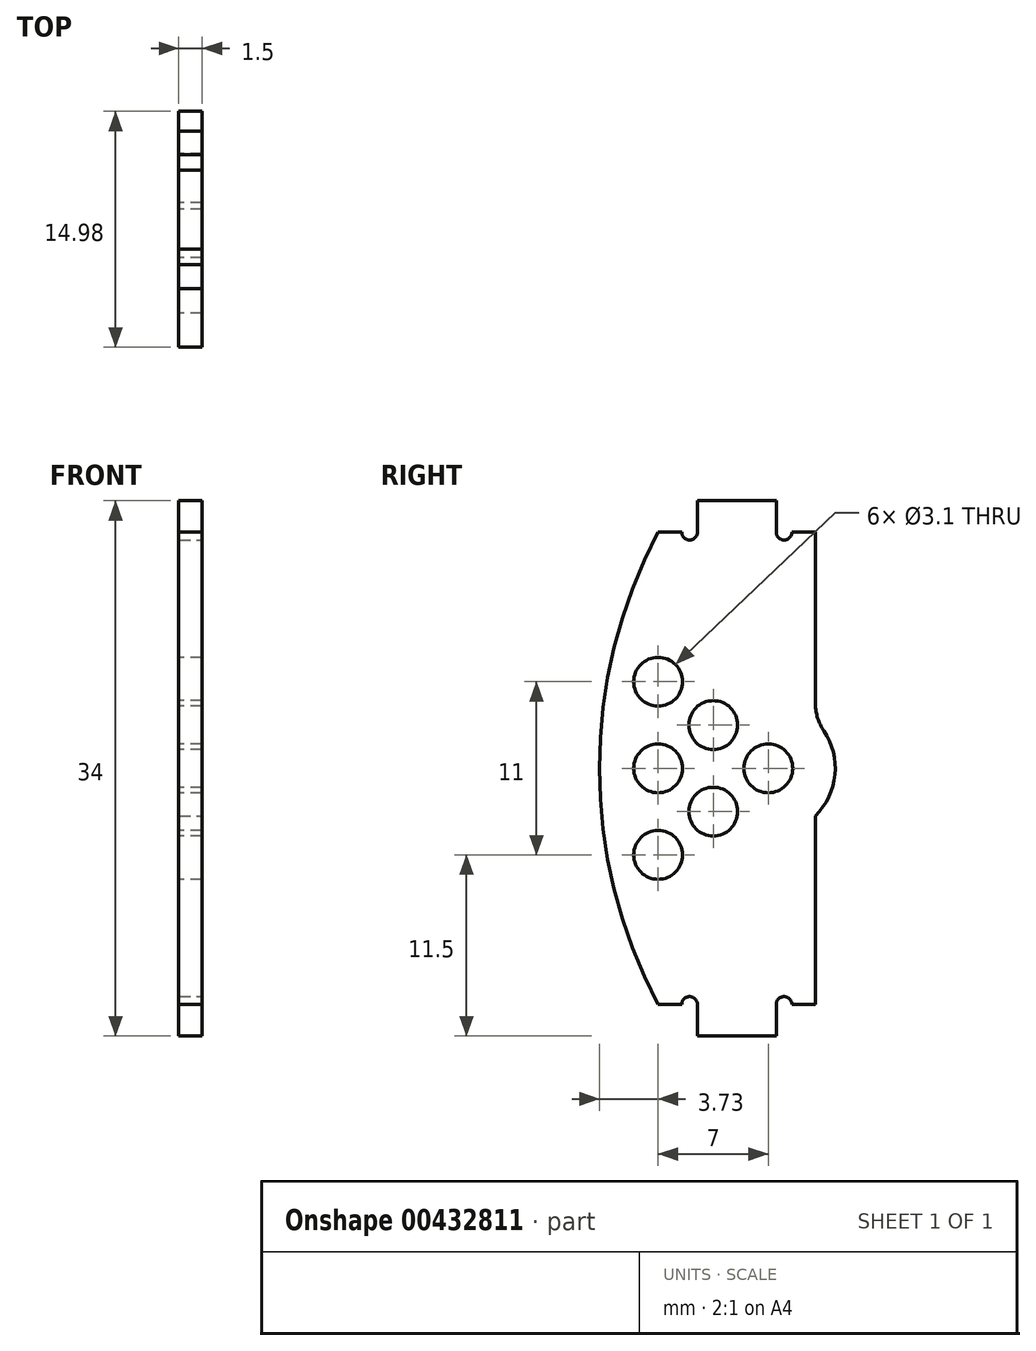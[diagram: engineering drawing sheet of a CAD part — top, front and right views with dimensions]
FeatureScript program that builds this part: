
annotation { "Feature Type Name" : "Feature", "Feature Type Description" : "" }
export const myFeature = defineFeature(function(context is Context, id is Id, definition is map)
    precondition{}
    {
        {
            var Q0;
            Q0=qCreatedBy(makeId("Right.planeOp"),FACE);
            var sketch = newSketch(context, id + "F0", { "sketchPlane" : qUnion([Q0])});
            skLineSegment(sketch, "E0", {"start": v(0, 0) * mm, "end": v(0, 30) * mm});
            skLineSegment(sketch, "E1", {"start": v(0, 30) * mm, "end": v(-10, 30) * mm});
            skLineSegment(sketch, "E2", {"start": v(0, 0) * mm, "end": v(-10, 0) * mm});
            skArc(sketch, "E3", {"start": v(-10, 30) * mm, "mid": v(-13.73, 15) * mm, "end": v(-10, 0) * mm});
            skCircle(sketch, "E4", {"center": v(-3, 15) * mm, "radius": 1.55 * mm});
            skLineSegment(sketch, "E5", {"start": v(-3, 15) * mm, "end": v(0, 15) * mm, "construction": true});
            skCircle(sketch, "E6", {"center": v(-10, 9.5) * mm, "radius": 1.55 * mm});
            skCircle(sketch, "E7.MirrorC", {"center": v(-10, 20.5) * mm, "radius": 1.55 * mm});
            skCircle(sketch, "E8", {"center": v(-6.5, 12.25) * mm, "radius": 1.55 * mm});
            skCircle(sketch, "E9.MirrorC", {"center": v(-6.5, 17.75) * mm, "radius": 1.55 * mm});
            skCircle(sketch, "E10", {"center": v(-10, 15) * mm, "radius": 1.55 * mm});
            skSolve(sketch);
        }
        {
            var Q0;
            Q0=makeQuery(id+"F0.imprint","IMPRINT",FACE,{"disambiguationData":[TD([[makeQuery(id+"F0.imprint","IMPRINT",EDGE,{"derivedFrom":sQuery(id+"F0.wireOp",EDGE,"E0")}),1.0]])]});
            extrude(context, id + "F1", {"entities" : qUnion([Q0]), "depth" : 1.5 * mm});
        }
        {
            var Q0;
            Q0=makeQuery(id+"F1.opExtrude","CAP_FACE",FACE,{"disambiguationData":[OSD([sQuery(id+"F0.wireOp",EDGE,"E0"),sQuery(id+"F0.wireOp",EDGE,"E1"),sQuery(id+"F0.wireOp",EDGE,"E2"),sQuery(id+"F0.wireOp",EDGE,"E3"),sQuery(id+"F0.wireOp",EDGE,"E4")])],"isStart":false});
            var sketch = newSketch(context, id + "F2", { "sketchPlane" : qUnion([Q0])});
            skLineSegment(sketch, "E11.bottom", {"start": v(-7.5, 30) * mm, "end": v(-2.5, 30) * mm});
            skLineSegment(sketch, "E11.top", {"start": v(-7.5, 32) * mm, "end": v(-2.5, 32) * mm});
            skLineSegment(sketch, "E11.left", {"start": v(-7.5, 30) * mm, "end": v(-7.5, 32) * mm});
            skLineSegment(sketch, "E11.right", {"start": v(-2.5, 30) * mm, "end": v(-2.5, 32) * mm});
            skLineSegment(sketch, "E12", {"start": v(-3, 15) * mm, "end": v(0, 15) * mm, "construction": true});
            skLineSegment(sketch, "E13.MirrorCS", {"start": v(-2.5, 0) * mm, "end": v(-2.5, -2) * mm});
            skLineSegment(sketch, "E14.MirrorCS", {"start": v(-7.5, 0) * mm, "end": v(-7.5, -2) * mm});
            skLineSegment(sketch, "E15.MirrorCS", {"start": v(-7.5, -2) * mm, "end": v(-2.5, -2) * mm});
            skLineSegment(sketch, "E16.MirrorCS", {"start": v(-7.5, 0) * mm, "end": v(-2.5, 0) * mm});
            skSolve(sketch);
        }
        {
            var Q0;
            Q0=makeQuery(id+"F2.imprint","IMPRINT",FACE,{"disambiguationData":[TD([[makeQuery(id+"F2.imprint","IMPRINT",EDGE,{"derivedFrom":sQuery(id+"F2.wireOp",EDGE,"E11.bottom")}),-1.0]])]});
            var Q1;
            Q1=makeQuery(id+"F2.imprint","IMPRINT",FACE,{"disambiguationData":[TD([[makeQuery(id+"F2.imprint","IMPRINT",EDGE,{"derivedFrom":sQuery(id+"F2.wireOp",EDGE,"E13.MirrorCS")}),-1.0]])]});
            extrude(context, id + "F3", {"entities" : qUnion([Q0, Q1]), "operationType" : NewBodyOperationType.ADD, "oppositeDirection" : true, "depth" : 1.5 * mm});
        }
        {
            var Q0;
            Q0=makeQuery(id+"F3.boolean.opBoolean","MERGE",FACE,{"derivedFrom":[makeQuery(id+"F1.opExtrude","CAP_FACE",FACE,{"disambiguationData":[OSD([sQuery(id+"F0.wireOp",EDGE,"E0"),sQuery(id+"F0.wireOp",EDGE,"E1"),sQuery(id+"F0.wireOp",EDGE,"E2"),sQuery(id+"F0.wireOp",EDGE,"E3"),sQuery(id+"F0.wireOp",EDGE,"E4")])],"isStart":false}),makeQuery(id+"F3.opExtrude","CAP_FACE",FACE,{"disambiguationData":[OSD([sQuery(id+"F2.wireOp",EDGE,"E11.bottom"),sQuery(id+"F2.wireOp",EDGE,"E11.top"),sQuery(id+"F2.wireOp",EDGE,"E11.left"),sQuery(id+"F2.wireOp",EDGE,"E11.right")])],"isStart":true}),makeQuery(id+"F3.opExtrude","CAP_FACE",FACE,{"disambiguationData":[OSD([sQuery(id+"F2.wireOp",EDGE,"E13.MirrorCS"),sQuery(id+"F2.wireOp",EDGE,"E14.MirrorCS"),sQuery(id+"F2.wireOp",EDGE,"E15.MirrorCS"),sQuery(id+"F2.wireOp",EDGE,"E16.MirrorCS")])],"isStart":true})]});
            var sketch = newSketch(context, id + "F4", { "sketchPlane" : qUnion([Q0])});
            skCircle(sketch, "E17", {"center": v(-8, 30) * mm, "radius": 0.5 * mm});
            skCircle(sketch, "E18", {"center": v(-2, 30) * mm, "radius": 0.5 * mm});
            skLineSegment(sketch, "E19", {"start": v(-3, 15) * mm, "end": v(0, 15) * mm, "construction": true});
            skCircle(sketch, "E20.MirrorC", {"center": v(-2, 0) * mm, "radius": 0.5 * mm});
            skCircle(sketch, "E21.MirrorC", {"center": v(-8, 0) * mm, "radius": 0.5 * mm});
            skSolve(sketch);
        }
        {
            var Q0;
            Q0 = qSketchRegion(id + "F4", true);
            extrude(context, id + "F5", {"entities" : qUnion([Q0]), "operationType" : NewBodyOperationType.REMOVE, "oppositeDirection" : true, "depth" : 25 * mm});
        }
        {
            var Q0;
            Q0=makeQuery(id+"F3.boolean.opBoolean","MERGE",FACE,{"derivedFrom":[makeQuery(id+"F1.opExtrude","CAP_FACE",FACE,{"disambiguationData":[OSD([sQuery(id+"F0.wireOp",EDGE,"E0"),sQuery(id+"F0.wireOp",EDGE,"E1"),sQuery(id+"F0.wireOp",EDGE,"E2"),sQuery(id+"F0.wireOp",EDGE,"E3"),sQuery(id+"F0.wireOp",EDGE,"E4"),sQuery(id+"F0.wireOp",EDGE,"E6")])],"isStart":false}),makeQuery(id+"F3.opExtrude","CAP_FACE",FACE,{"disambiguationData":[OSD([sQuery(id+"F2.wireOp",EDGE,"E11.bottom"),sQuery(id+"F2.wireOp",EDGE,"E11.top"),sQuery(id+"F2.wireOp",EDGE,"E11.left"),sQuery(id+"F2.wireOp",EDGE,"E11.right")])],"isStart":true}),makeQuery(id+"F3.opExtrude","CAP_FACE",FACE,{"disambiguationData":[OSD([sQuery(id+"F2.wireOp",EDGE,"E13.MirrorCS"),sQuery(id+"F2.wireOp",EDGE,"E14.MirrorCS"),sQuery(id+"F2.wireOp",EDGE,"E15.MirrorCS"),sQuery(id+"F2.wireOp",EDGE,"E16.MirrorCS")])],"isStart":true})]});
            var sketch = newSketch(context, id + "F6", { "sketchPlane" : qUnion([Q0])});
            skArc(sketch, "E22", {"start": v(0, 11.99) * mm, "mid": v(1.25, 15) * mm, "end": v(0, 18.01) * mm});
            skLineSegment(sketch, "E23", {"start": v(0, 18.01) * mm, "end": v(0, 11.99) * mm});
            skSolve(sketch);
        }
        {
            var Q0;
            Q0=makeQuery(id+"F6.imprint","IMPRINT",FACE,{"disambiguationData":[TD([[makeQuery(id+"F6.imprint","IMPRINT",EDGE,{"derivedFrom":sQuery(id+"F6.wireOp",EDGE,"E22")}),1.0]])]});
            extrude(context, id + "F7", {"entities" : qUnion([Q0]), "operationType" : NewBodyOperationType.ADD, "oppositeDirection" : true, "depth" : 1.5 * mm});
        }
        {
            var Q0;
            {var subQ0=sQuery(id+"F6.wireOp",EDGE,"E23");var subQ1=sQuery(id+"F6.wireOp",EDGE,"E22");var subQ2=sQuery(id+"F0.wireOp",EDGE,"E0");Q0=makeQuery(id+"F7.opExtrude","SWEPT_EDGE",EDGE,{"disambiguationData":[OSD([subQ2,subQ1,subQ0]),TDD([makeQuery(id+"F6.imprint","INTERSECT",VERTEX,{"disambiguationData":[OD(1.0)],"derivedFrom":[makeQuery(id+"F1.opExtrude","CAP_EDGE",EDGE,{"disambiguationData":[OSD([subQ2])],"isStart":false}),subQ1,subQ0]})])]});}
            var Q1;
            {var subQ0=sQuery(id+"F6.wireOp",EDGE,"E23");var subQ1=sQuery(id+"F6.wireOp",EDGE,"E22");var subQ2=sQuery(id+"F0.wireOp",EDGE,"E0");Q1=makeQuery(id+"F7.opExtrude","SWEPT_EDGE",EDGE,{"disambiguationData":[OSD([subQ2,subQ1,subQ0]),TDD([makeQuery(id+"F6.imprint","INTERSECT",VERTEX,{"disambiguationData":[OD(0.0)],"derivedFrom":[makeQuery(id+"F1.opExtrude","CAP_EDGE",EDGE,{"disambiguationData":[OSD([subQ2])],"isStart":false}),subQ1,subQ0]})])]});}
            fillet(context, id + "F8", {"entities" : qUnion([Q0, Q1]), "radius" : 3 * mm, "tangentPropagation" : true, "allowEdgeOverflow" : false});
        }
    });
